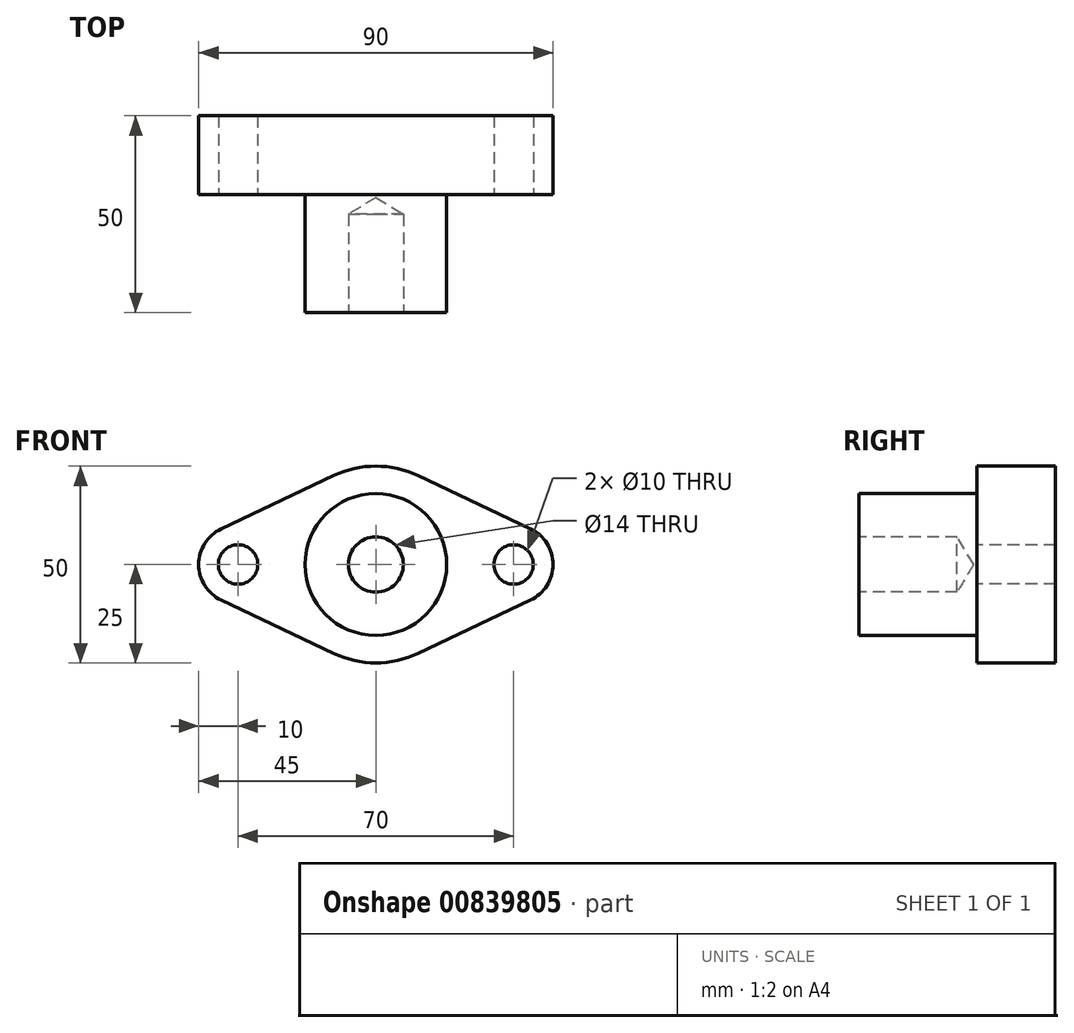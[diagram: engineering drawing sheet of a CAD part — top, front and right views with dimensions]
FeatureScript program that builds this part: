
annotation { "Feature Type Name" : "Feature", "Feature Type Description" : "" }
export const myFeature = defineFeature(function(context is Context, id is Id, definition is map)
    precondition{}
    {
        {
            var Q0;
            Q0=qCreatedBy(makeId("Front.planeOp"),FACE);
            var sketch = newSketch(context, id + "F0", { "sketchPlane" : qUnion([Q0])});
            skCircle(sketch, "E0", {"center": v(0, 0) * mm, "radius": 25 * mm});
            skPoint(sketch, "E1", {"position": v(-35, 0) * mm});
            skPoint(sketch, "E2", {"position": v(35, 0) * mm});
            skCircle(sketch, "E3", {"center": v(-35, 0) * mm, "radius": 10 * mm});
            skCircle(sketch, "E4", {"center": v(35, 0) * mm, "radius": 10 * mm});
            skLineSegment(sketch, "E5", {"start": v(-39.29, 9.04) * mm, "end": v(-10.71, 22.59) * mm});
            skLineSegment(sketch, "E6", {"start": v(39.29, -9.04) * mm, "end": v(10.71, -22.59) * mm});
            skLineSegment(sketch, "E7", {"start": v(-39.29, -9.04) * mm, "end": v(-10.71, -22.59) * mm});
            skLineSegment(sketch, "E8.trimOffspring", {"start": v(10.71, 22.59) * mm, "end": v(39.29, 9.04) * mm});
            skSolve(sketch);
        }
        {
            var Q0;
            {var subQ0=sQuery(id+"F0.wireOp",EDGE,"E5");Q0=makeQuery(id+"F0.imprint","IMPRINT",FACE,{"disambiguationData":[TD([[makeQuery(id+"F0.imprint","IMPRINT",EDGE,{"derivedFrom":subQ0}),-1.0]])]});}
            var Q1;
            {var subQ0=sQuery(id+"F0.wireOp",EDGE,"E6");Q1=makeQuery(id+"F0.imprint","IMPRINT",FACE,{"disambiguationData":[TD([[makeQuery(id+"F0.imprint","IMPRINT",EDGE,{"derivedFrom":subQ0}),-1.0]])]});}
            var Q2;
            {var subQ0=sQuery(id+"F0.wireOp",EDGE,"E7");Q2=makeQuery(id+"F0.imprint","IMPRINT",FACE,{"disambiguationData":[TD([[makeQuery(id+"F0.imprint","IMPRINT",EDGE,{"derivedFrom":subQ0}),1.0]])]});}
            var Q3;
            {var subQ0=sQuery(id+"F0.wireOp",EDGE,"E0");var subQ4=makeQuery(id+"F0.imprint","INTERSECT",VERTEX,{"derivedFrom":[subQ0,sQuery(id+"F0.wireOp",EDGE,"E8.trimOffspring")]});Q3=makeQuery(id+"F0.imprint","IMPRINT",FACE,{"disambiguationData":[TD([[makeQuery(id+"F0.imprint","IMPRINT",EDGE,{"disambiguationData":[TD([[subQ4,1.0]])],"derivedFrom":subQ0}),1.0]])]});}
            var Q4;
            {var subQ0=sQuery(id+"F0.wireOp",EDGE,"E3");var subQ1=makeQuery(id+"F0.imprint","INTERSECT",VERTEX,{"derivedFrom":[subQ0,sQuery(id+"F0.wireOp",EDGE,"E5")]});Q4=makeQuery(id+"F0.imprint","IMPRINT",FACE,{"disambiguationData":[TD([[makeQuery(id+"F0.imprint","IMPRINT",EDGE,{"disambiguationData":[TD([[subQ1,1.0]])],"derivedFrom":subQ0}),1.0]])]});}
            var Q5;
            {var subQ0=sQuery(id+"F0.wireOp",EDGE,"E4");var subQ1=makeQuery(id+"F0.imprint","INTERSECT",VERTEX,{"derivedFrom":[subQ0,sQuery(id+"F0.wireOp",EDGE,"E8.trimOffspring")]});Q5=makeQuery(id+"F0.imprint","IMPRINT",FACE,{"disambiguationData":[TD([[makeQuery(id+"F0.imprint","IMPRINT",EDGE,{"disambiguationData":[TD([[subQ1,-1.0]])],"derivedFrom":subQ0}),1.0]])]});}
            var Q6;
            {var subQ0=sQuery(id+"F0.wireOp",EDGE,"E8.trimOffspring");Q6=makeQuery(id+"F0.imprint","IMPRINT",FACE,{"disambiguationData":[TD([[makeQuery(id+"F0.imprint","IMPRINT",EDGE,{"derivedFrom":subQ0}),-1.0]])]});}
            extrude(context, id + "F1", {"entities" : qUnion([Q0, Q1, Q2, Q3, Q4, Q5, Q6]), "depth" : 20 * mm, "offsetDistance" : 25 * mm});
        }
        {
            var Q0;
            Q0=makeQuery(id+"F1.opExtrude","CAP_FACE",FACE,{"disambiguationData":[OSD([sQuery(id+"F0.wireOp",EDGE,"E0"),sQuery(id+"F0.wireOp",EDGE,"E3"),sQuery(id+"F0.wireOp",EDGE,"E4"),sQuery(id+"F0.wireOp",EDGE,"E5"),sQuery(id+"F0.wireOp",EDGE,"E6"),sQuery(id+"F0.wireOp",EDGE,"E7"),sQuery(id+"F0.wireOp",EDGE,"E8.trimOffspring")])],"isStart":false});
            var sketch = newSketch(context, id + "F2", { "sketchPlane" : qUnion([Q0])});
            skPoint(sketch, "E9", {"position": v(-35, 0) * mm});
            skPoint(sketch, "E10", {"position": v(35, 0) * mm});
            skCircle(sketch, "E11", {"center": v(0, 0) * mm, "radius": 18 * mm});
            skSolve(sketch);
        }
        {
            var Q0;
            Q0=sQuery(id+"F2.wireOp",VERTEX,"E9");
            var Q1;
            Q1=sQuery(id+"F2.wireOp",VERTEX,"E10");
            var Q2;
            Q2=makeQuery(id+"F1.opExtrude","SWEPT_BODY",BODY,{"disambiguationData":[OSD([sQuery(id+"F0.wireOp",EDGE,"E0"),sQuery(id+"F0.wireOp",EDGE,"E3"),sQuery(id+"F0.wireOp",EDGE,"E4"),sQuery(id+"F0.wireOp",EDGE,"E5"),sQuery(id+"F0.wireOp",EDGE,"E6"),sQuery(id+"F0.wireOp",EDGE,"E7"),sQuery(id+"F0.wireOp",EDGE,"E8.trimOffspring")])]});
            hole(context, id + "F3", {"style" : HoleStyle.SIMPLE, "endStyle" : HoleEndStyle.THROUGH, "holeDiameter" : 10 * mm, "majorDiameter" : 5 * mm, "isTappedThrough" : true, "tappedDepth" : 12 * mm, "tapClearance" : 3, "locations" : qUnion([Q0, Q1]), "scope" : qUnion([Q2])});
        }
        {
            var Q0;
            Q0 = qSketchRegion(id + "F2", true);
            extrude(context, id + "F4", {"entities" : qUnion([Q0]), "operationType" : NewBodyOperationType.ADD, "depth" : 30 * mm, "offsetDistance" : 25 * mm});
        }
        {
            var Q0;
            Q0=makeQuery(id+"F4.opExtrude","CAP_FACE",FACE,{"disambiguationData":[OSD([sQuery(id+"F2.wireOp",EDGE,"E11")])],"isStart":false});
            var sketch = newSketch(context, id + "F5", { "sketchPlane" : qUnion([Q0])});
            skPoint(sketch, "E12", {"position": v(0, 0) * mm});
            skSolve(sketch);
        }
        {
            var Q0;
            Q0=sQuery(id+"F5.wireOp",VERTEX,"E12");
            var Q1;
            Q1=makeQuery(id+"F1.opExtrude","SWEPT_BODY",BODY,{"disambiguationData":[OSD([sQuery(id+"F0.wireOp",EDGE,"E0"),sQuery(id+"F0.wireOp",EDGE,"E3"),sQuery(id+"F0.wireOp",EDGE,"E4"),sQuery(id+"F0.wireOp",EDGE,"E5"),sQuery(id+"F0.wireOp",EDGE,"E6"),sQuery(id+"F0.wireOp",EDGE,"E7"),sQuery(id+"F0.wireOp",EDGE,"E8.trimOffspring")])]});
            hole(context, id + "F6", {"style" : HoleStyle.SIMPLE, "endStyle" : HoleEndStyle.BLIND, "standardTappedOrClearance" : lookupTablePath({ "standard" : "ISO", "engagement" : "75%", "pitch" : "2 mm", "size" : "M16", "type" : "Tapped" }), "standardBlindInLast" : lookupTablePath({ "standard" : "ISO", "engagement" : "75%", "pitch" : "2 mm", "size" : "M16", "type" : "Tapped" }), "holeDiameter" : 14 * mm, "majorDiameter" : 16 * mm, "showTappedDepth" : true, "holeDepth" : 25 * mm, "isTappedThrough" : true, "tappedDepth" : 19 * mm, "tapClearance" : 3, "locations" : qUnion([Q0]), "scope" : qUnion([Q1])});
        }
    });
